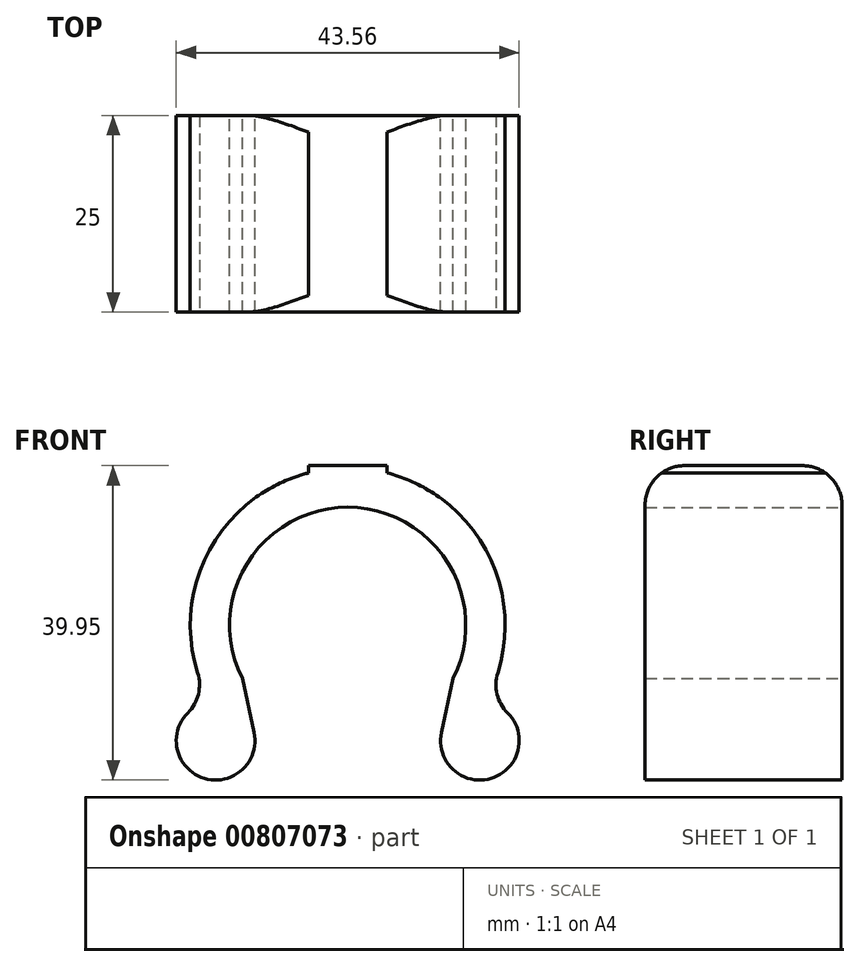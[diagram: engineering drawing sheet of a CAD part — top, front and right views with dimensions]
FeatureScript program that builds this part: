
annotation { "Feature Type Name" : "Feature", "Feature Type Description" : "" }
export const myFeature = defineFeature(function(context is Context, id is Id, definition is map)
    precondition{}
    {
        {
            var Q0;
            Q0=qCreatedBy(makeId("Front.planeOp"),FACE);
            var sketch = newSketch(context, id + "F0", { "sketchPlane" : qUnion([Q0])});
            skArc(sketch, "E0", {"start": v(17.48, -9.71) * mm, "mid": v(18.38, 7.89) * mm, "end": v(5, 19.36) * mm});
            skArc(sketch, "E1", {"start": v(13.4, -6.76) * mm, "mid": v(12.77, 7.86) * mm, "end": v(0, 15) * mm});
            skLineSegment(sketch, "E2", {"start": v(0, 20) * mm, "end": v(0, 15) * mm});
            skLineSegment(sketch, "E3", {"start": v(13.4, -6.76) * mm, "end": v(11.9, -13.6) * mm});
            skArc(sketch, "E4", {"start": v(11.9, -13.6) * mm, "mid": v(19.64, -18.77) * mm, "end": v(17.48, -9.71) * mm});
            skLineSegment(sketch, "E5", {"start": v(0, 59.54) * mm, "end": v(0, 69.88) * mm});
            skLineSegment(sketch, "E6", {"start": v(0, -9.02) * mm, "end": v(0, 85.69) * mm, "construction": true});
            skLineSegment(sketch, "E7", {"start": v(0, 59.54) * mm, "end": v(0, 54.54) * mm});
            skLineSegment(sketch, "E8", {"start": v(0, 29.54) * mm, "end": v(0, 34.54) * mm});
            skLineSegment(sketch, "E9", {"start": v(0, 29.54) * mm, "end": v(0, 20) * mm});
            skLineSegment(sketch, "E10", {"start": v(5, 19.36) * mm, "end": v(5, 20.28) * mm});
            skLineSegment(sketch, "E11", {"start": v(5, 20.28) * mm, "end": v(0, 20.28) * mm});
            skSolve(sketch);
        }
        {
            var Q0;
            Q0=qSketchRegion(id+"F0",true);
            extrude(context, id + "F1", {"entities" : qUnion([Q0]), "depth" : 25 * mm, "offsetDistance" : 25 * mm});
        }
        {
            var Q0;
            Q0=makeQuery(id+"F1.opExtrude","SWEPT_BODY",BODY,{"disambiguationData":[OSD([sQuery(id+"F0.wireOp",EDGE,"E0"),sQuery(id+"F0.wireOp",EDGE,"E1"),sQuery(id+"F0.wireOp",EDGE,"E2"),sQuery(id+"F0.wireOp",EDGE,"E3"),sQuery(id+"F0.wireOp",EDGE,"E4")])]});
            var Q1;
            Q1=makeQuery(id+"F1.opExtrude","SWEPT_BODY",BODY,{"disambiguationData":[OSD([sQuery(id+"F0.wireOp",EDGE,"ZJeOtKvS-0V8n-BAj4-BAVA-AoswjEcr5JXE"),sQuery(id+"F0.wireOp",EDGE,"GTKcsJUI-YMfE-Q9Rm-PllJ-e9fJrtKgK9LG"),sQuery(id+"F0.wireOp",EDGE,"ZKlF4mqJ-5DrE-eTdW-whtT-mimaQSIe7lm9"),sQuery(id+"F0.wireOp",EDGE,"B9OKSv2O-DWHs-XMQp-p7Ia-sCPH9sulsA8u"),sQuery(id+"F0.wireOp",EDGE,"7JTtOB6v-8xqh-fVU6-w0FL-nSfP0XwtOn2y"),sQuery(id+"F0.wireOp",EDGE,"698f7dfc-63ae-4ce6-86f1-02b924555ac6.filletArc"),sQuery(id+"F0.wireOp",EDGE,"46WvWRZJ-fj3N-dYTW-aIvH-BbHphLMpPgnm"),sQuery(id+"F0.wireOp",EDGE,"E7"),sQuery(id+"F0.wireOp",EDGE,"E8")])]});
            var Q2;
            Q2=qCreatedBy(makeId("Right.planeOp"),FACE);
            mirror(context, id + "F2", {"operationType" : NewBodyOperationType.ADD, "entities" : qUnion([Q0, Q1]), "mirrorPlane" : qUnion([Q2])});
        }
        {
            var Q0;
            Q0=makeQuery(id+"F2.opPattern","COPY",EDGE,{"derivedFrom":makeQuery(id+"F1.opExtrude","CAP_EDGE",EDGE,{"disambiguationData":[OSD([sQuery(id+"F0.wireOp",EDGE,"GTKcsJUI-YMfE-Q9Rm-PllJ-e9fJrtKgK9LG")])],"isStart":false}),"instanceName":"1"});
            var Q1;
            Q1=makeQuery(id+"F1.opExtrude","CAP_EDGE",EDGE,{"disambiguationData":[OSD([sQuery(id+"F0.wireOp",EDGE,"GTKcsJUI-YMfE-Q9Rm-PllJ-e9fJrtKgK9LG")])],"isStart":false});
            var Q2;
            Q2=makeQuery(id+"F1.opExtrude","CAP_EDGE",EDGE,{"disambiguationData":[OSD([sQuery(id+"F0.wireOp",EDGE,"GTKcsJUI-YMfE-Q9Rm-PllJ-e9fJrtKgK9LG")])],"isStart":true});
            var Q3;
            Q3=makeQuery(id+"F2.opPattern","COPY",EDGE,{"derivedFrom":makeQuery(id+"F1.opExtrude","CAP_EDGE",EDGE,{"disambiguationData":[OSD([sQuery(id+"F0.wireOp",EDGE,"GTKcsJUI-YMfE-Q9Rm-PllJ-e9fJrtKgK9LG")])],"isStart":true}),"instanceName":"1"});
            var Q4;
            Q4=makeQuery(id+"F1.opExtrude","CAP_EDGE",EDGE,{"disambiguationData":[OSD([sQuery(id+"F0.wireOp",EDGE,"N7nh7c8y-5UWk-OEKt-zLoe-UIArFTChwELI")])],"isStart":true});
            var Q5;
            Q5=makeQuery(id+"F2.opPattern","COPY",EDGE,{"derivedFrom":makeQuery(id+"F1.opExtrude","CAP_EDGE",EDGE,{"disambiguationData":[OSD([sQuery(id+"F0.wireOp",EDGE,"N7nh7c8y-5UWk-OEKt-zLoe-UIArFTChwELI")])],"isStart":true}),"instanceName":"1"});
            var Q6;
            Q6=makeQuery(id+"F2.opPattern","COPY",EDGE,{"derivedFrom":makeQuery(id+"F1.opExtrude","CAP_EDGE",EDGE,{"disambiguationData":[OSD([sQuery(id+"F0.wireOp",EDGE,"N7nh7c8y-5UWk-OEKt-zLoe-UIArFTChwELI")])],"isStart":false}),"instanceName":"1"});
            var Q7;
            Q7=makeQuery(id+"F1.opExtrude","CAP_EDGE",EDGE,{"disambiguationData":[OSD([sQuery(id+"F0.wireOp",EDGE,"N7nh7c8y-5UWk-OEKt-zLoe-UIArFTChwELI")])],"isStart":false});
            var Q8;
            Q8=makeQuery(id+"F2.opPattern","COPY",EDGE,{"derivedFrom":makeQuery(id+"F1.opExtrude","SWEPT_EDGE",EDGE,{"disambiguationData":[OSD([sQuery(id+"F0.wireOp",EDGE,"E0"),sQuery(id+"F0.wireOp",EDGE,"E4")])]}),"instanceName":"1"});
            var Q9;
            Q9=makeQuery(id+"F1.opExtrude","SWEPT_EDGE",EDGE,{"disambiguationData":[OSD([sQuery(id+"F0.wireOp",EDGE,"E0"),sQuery(id+"F0.wireOp",EDGE,"E4")])]});
            var Q10;
            {var subQ0=makeQuery(id+"F1.opExtrude","CAP_EDGE",EDGE,{"disambiguationData":[OSD([sQuery(id+"F0.wireOp",EDGE,"E11")])],"isStart":false});Q10=makeQuery(id+"F2.boolean.opBoolean","MERGE",EDGE,{"derivedFrom":[subQ0,makeQuery(id+"F2.opPattern","COPY",EDGE,{"derivedFrom":subQ0,"instanceName":"1"})]});}
            var Q11;
            {var subQ0=makeQuery(id+"F1.opExtrude","CAP_EDGE",EDGE,{"disambiguationData":[OSD([sQuery(id+"F0.wireOp",EDGE,"E11")])],"isStart":true});Q11=makeQuery(id+"F2.boolean.opBoolean","MERGE",EDGE,{"derivedFrom":[subQ0,makeQuery(id+"F2.opPattern","COPY",EDGE,{"derivedFrom":subQ0,"instanceName":"1"})]});}
            fillet(context, id + "F3", {"entities" : qUnion([Q0, Q1, Q2, Q3, Q4, Q5, Q6, Q7, Q8, Q9, Q10, Q11]), "radius" : 5 * mm, "tangentPropagation" : true, "allowEdgeOverflow" : false});
        }
    });
